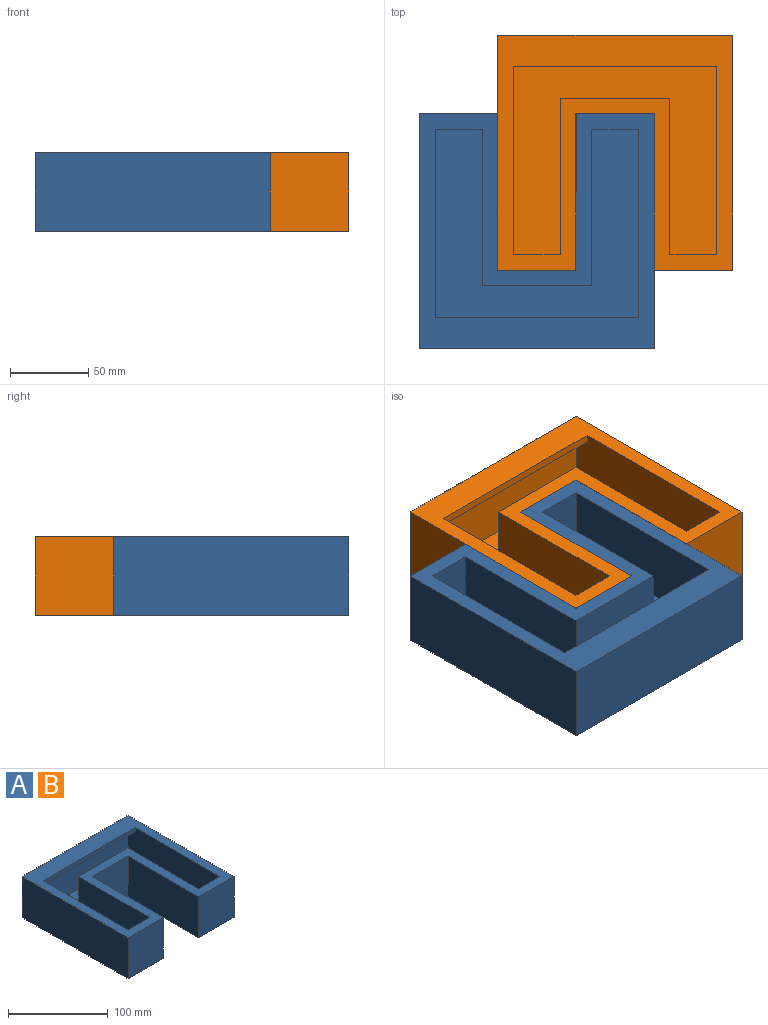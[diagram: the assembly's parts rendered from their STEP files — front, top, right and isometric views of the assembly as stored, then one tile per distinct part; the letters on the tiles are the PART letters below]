
ASSEMBLY  parts=2 mates=1
PART A: 21 faces, bbox 150x150x50 mm
  f0: plane 130x40mm, normal (0,-1,0), area 5200mm2, adj f1,f10,f18,f19
  f1: plane 130x45mm, normal (-1,0,0), area 5800mm2, adj f0,f11,f17,f18,f19,f20
  f2: plane 150x150mm, normal (0,0,-1), area 17500mm2, adj f3,f4,f5,f6,f7,f8,f9,f16
  f3: plane 150x50mm, normal (-1,0,0), area 7500mm2, adj f2,f4,f16,f17
  f4: plane 50x50mm, normal (0,-1,0), area 2500mm2, adj f2,f3,f5,f17
  f5: plane 100x50mm, normal (1,0,0), area 5000mm2, adj f2,f4,f6,f17
  f6: plane 50x50mm, normal (0,-1,0), area 2500mm2, adj f2,f5,f7,f17
  f7: plane 100x50mm, normal (-1,0,0), area 5000mm2, adj f2,f6,f8,f17
  f8: plane 50x50mm, normal (0,-1,0), area 2500mm2, adj f2,f7,f9,f17
  f9: plane 150x50mm, normal (1,0,0), area 7500mm2, adj f2,f8,f16,f17
  f10: plane 130x45mm, normal (1,0,0), area 5800mm2, adj f0,f15,f17,f18,f19,f20
  f11: plane 45x30mm, normal (0,1,0), area 1350mm2, adj f1,f12,f17,f18
  f12: plane 100x45mm, normal (1,0,0), area 4500mm2, adj f11,f13,f17,f18
  f13: plane 70x45mm, normal (0,1,0), area 3150mm2, adj f12,f14,f17,f18
  f14: plane 100x45mm, normal (-1,0,0), area 4500mm2, adj f13,f15,f17,f18
  f15: plane 45x30mm, normal (0,1,0), area 1350mm2, adj f10,f14,f17,f18
  f16: plane 150x50mm, normal (0,1,0), area 7500mm2, adj f2,f3,f9,f17
  f17: plane 150x150mm, normal (0,0,1), area 8900mm2, adj f1,f3,f4,f5,f6,f7,f8,f9
  f18: plane 130x130mm, normal (0,0,1), area 9900mm2, adj f0,f1,f10,f11,f12,f13,f14,f15
  f19: plane 130x10mm, normal (0,0,-1), area 1300mm2, adj f0,f1,f10,f20
  f20: plane 130x5mm, normal (0,-1,0), area 650mm2, adj f1,f10,f17,f19
PART B: same geometry as A
PLACE A rot(axis=(0,0,-1),180deg) t=(-109.77,163.31,72.99)mm
PLACE B t=(90.23,63.31,72.99)mm
MATE fastened B.f4 <-> A.f6  axis (0,-1,0) through (-34.77,63.31,97.99)mm
